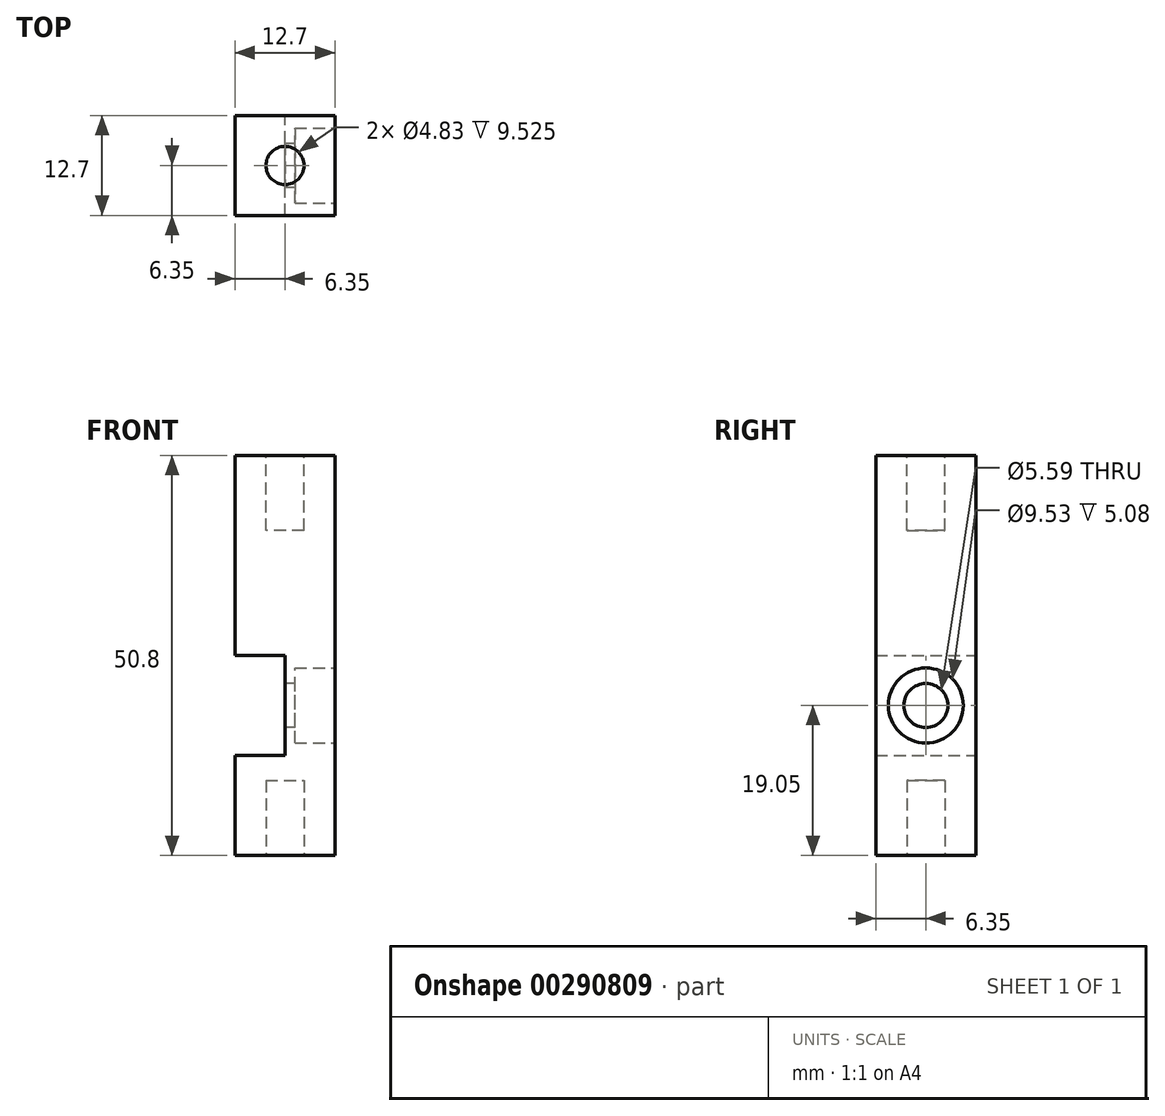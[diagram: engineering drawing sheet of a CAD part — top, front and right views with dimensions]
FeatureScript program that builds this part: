
annotation { "Feature Type Name" : "Feature", "Feature Type Description" : "" }
export const myFeature = defineFeature(function(context is Context, id is Id, definition is map)
    precondition{}
    {
        {
            var Q0;
            Q0=qCreatedBy(makeId("Right.planeOp"),FACE);
            var sketch = newSketch(context, id + "F0", { "sketchPlane" : qUnion([Q0])});
            skLineSegment(sketch, "E0.bottom", {"start": v(-12.7, 25.4) * mm, "end": v(0, 25.4) * mm});
            skLineSegment(sketch, "E0.top", {"start": v(-12.7, -25.4) * mm, "end": v(0, -25.4) * mm});
            skLineSegment(sketch, "E0.left", {"start": v(-12.7, 25.4) * mm, "end": v(-12.7, -25.4) * mm});
            skLineSegment(sketch, "E0.right", {"start": v(0, 25.4) * mm, "end": v(0, -25.4) * mm});
            skSolve(sketch);
        }
        {
            var Q0;
            Q0 = qSketchRegion(id + "F0", true);
            extrude(context, id + "F1", {"entities" : qUnion([Q0]), "depth" : 12.7 * mm});
        }
        {
            var Q0;
            Q0=makeQuery(id+"F1.opExtrude","SWEPT_FACE",FACE,{"disambiguationData":[OSD([sQuery(id+"F0.wireOp",EDGE,"E0.right")])]});
            var sketch = newSketch(context, id + "F2", { "sketchPlane" : qUnion([Q0])});
            skLineSegment(sketch, "E1.bottom", {"start": v(-6.35, 0) * mm, "end": v(0, 0) * mm});
            skLineSegment(sketch, "E1.top", {"start": v(-6.35, -12.7) * mm, "end": v(0, -12.7) * mm});
            skLineSegment(sketch, "E1.left", {"start": v(-6.35, 0) * mm, "end": v(-6.35, -12.7) * mm});
            skLineSegment(sketch, "E1.right", {"start": v(0, 0) * mm, "end": v(0, -12.7) * mm});
            skSolve(sketch);
        }
        {
            var Q0;
            Q0 = qSketchRegion(id + "F2", true);
            extrude(context, id + "F3", {"entities" : qUnion([Q0]), "operationType" : NewBodyOperationType.REMOVE, "endBound" : BoundingType.THROUGH_ALL, "oppositeDirection" : true, "depth" : 25.4 * mm});
        }
        {
            var Q0;
            Q0=makeQuery(id+"F3.boolean.opBoolean","COPY",FACE,{"derivedFrom":makeQuery(id+"F3.opExtrude","SWEPT_FACE",FACE,{"disambiguationData":[OSD([sQuery(id+"F2.wireOp",EDGE,"E1.left")])]})});
            var sketch = newSketch(context, id + "F4", { "sketchPlane" : qUnion([Q0])});
            skCircle(sketch, "E2", {"center": v(6.35, -6.35) * mm, "radius": 2.8 * mm});
            skSolve(sketch);
        }
        {
            var Q0;
            Q0 = qSketchRegion(id + "F4", true);
            extrude(context, id + "F5", {"entities" : qUnion([Q0]), "operationType" : NewBodyOperationType.REMOVE, "endBound" : BoundingType.THROUGH_ALL, "oppositeDirection" : true, "depth" : 25.4 * mm});
        }
        {
            var Q0;
            Q0=makeQuery(id+"F1.opExtrude","CAP_FACE",FACE,{"disambiguationData":[OSD([sQuery(id+"F0.wireOp",EDGE,"E0.bottom"),sQuery(id+"F0.wireOp",EDGE,"E0.top"),sQuery(id+"F0.wireOp",EDGE,"E0.left"),sQuery(id+"F0.wireOp",EDGE,"E0.right")])],"isStart":false});
            var sketch = newSketch(context, id + "F6", { "sketchPlane" : qUnion([Q0])});
            skCircle(sketch, "E3", {"center": v(-6.35, -6.35) * mm, "radius": 4.76 * mm});
            skSolve(sketch);
        }
        {
            var Q0;
            Q0 = qSketchRegion(id + "F6", true);
            extrude(context, id + "F7", {"entities" : qUnion([Q0]), "operationType" : NewBodyOperationType.REMOVE, "oppositeDirection" : true, "depth" : 5.08 * mm});
        }
        {
            var Q0;
            Q0=makeQuery(id+"F1.opExtrude","SWEPT_FACE",FACE,{"disambiguationData":[OSD([sQuery(id+"F0.wireOp",EDGE,"E0.bottom")])]});
            var sketch = newSketch(context, id + "F8", { "sketchPlane" : qUnion([Q0])});
            skCircle(sketch, "E4", {"center": v(6.35, -6.35) * mm, "radius": 2.41 * mm});
            skSolve(sketch);
        }
        {
            var Q0;
            Q0 = qSketchRegion(id + "F8", true);
            extrude(context, id + "F9", {"entities" : qUnion([Q0]), "operationType" : NewBodyOperationType.REMOVE, "oppositeDirection" : true, "depth" : 9.52 * mm});
        }
        {
            var Q0;
            Q0=makeQuery(id+"F1.opExtrude","SWEPT_FACE",FACE,{"disambiguationData":[OSD([sQuery(id+"F0.wireOp",EDGE,"E0.top")])]});
            var sketch = newSketch(context, id + "F10", { "sketchPlane" : qUnion([Q0])});
            skCircle(sketch, "E5", {"center": v(6.35, 6.35) * mm, "radius": 2.41 * mm});
            skSolve(sketch);
        }
        {
            var Q0;
            Q0 = qSketchRegion(id + "F10", true);
            extrude(context, id + "F11", {"entities" : qUnion([Q0]), "operationType" : NewBodyOperationType.REMOVE, "oppositeDirection" : true, "depth" : 9.52 * mm});
        }
    });
